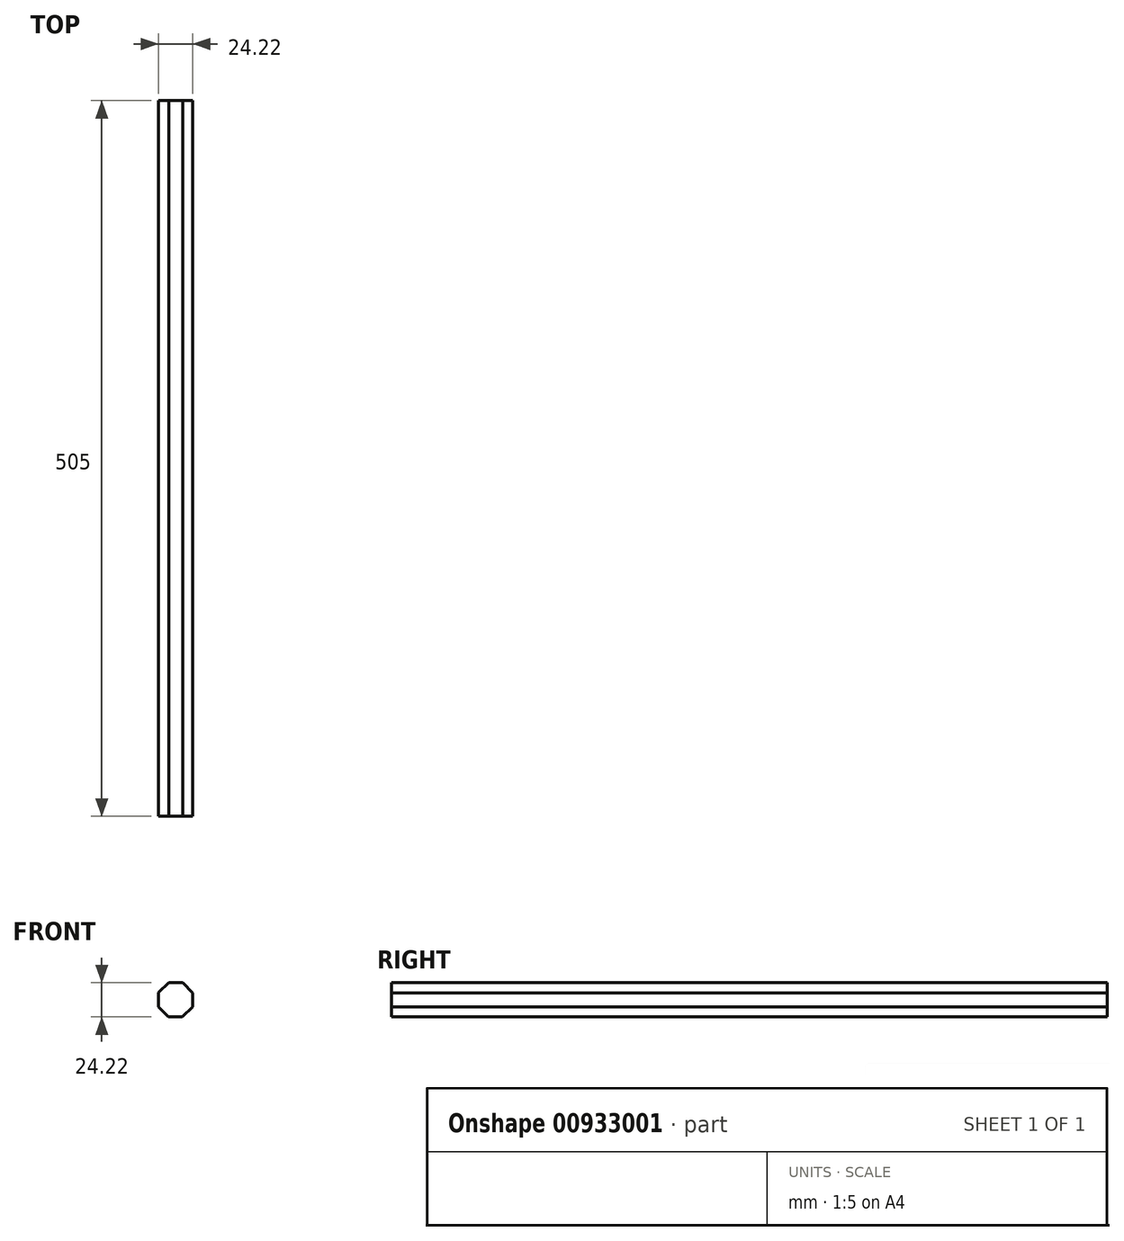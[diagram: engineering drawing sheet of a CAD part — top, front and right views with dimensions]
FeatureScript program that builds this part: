
annotation { "Feature Type Name" : "Feature", "Feature Type Description" : "" }
export const myFeature = defineFeature(function(context is Context, id is Id, definition is map)
    precondition{}
    {
        {
            var Q0;
            Q0=qCreatedBy(makeId("Front.planeOp"),FACE);
            var sketch = newSketch(context, id + "F0", { "sketchPlane" : qUnion([Q0])});
            skCircle(sketch, "E0.cCircle", {"center": v(0, 0) * mm, "radius": 12.07 * mm, "construction": true});
            skLineSegment(sketch, "E0.0", {"start": v(12.03, -5.1) * mm, "end": v(4.9, -12.1) * mm});
            skLineSegment(sketch, "E0.1", {"start": v(4.9, -12.1) * mm, "end": v(-5.1, -12.03) * mm});
            skLineSegment(sketch, "E0.2", {"start": v(-5.1, -12.03) * mm, "end": v(-12.1, -4.9) * mm});
            skLineSegment(sketch, "E0.3", {"start": v(-12.1, -4.9) * mm, "end": v(-12.03, 5.1) * mm});
            skLineSegment(sketch, "E0.4", {"start": v(-12.03, 5.1) * mm, "end": v(-4.9, 12.1) * mm});
            skLineSegment(sketch, "E0.5", {"start": v(-4.9, 12.1) * mm, "end": v(5.1, 12.03) * mm});
            skLineSegment(sketch, "E0.6", {"start": v(5.1, 12.03) * mm, "end": v(12.1, 4.9) * mm});
            skLineSegment(sketch, "E0.7", {"start": v(12.1, 4.9) * mm, "end": v(12.03, -5.1) * mm});
            skPoint(sketch, "E0.0.midPoint", {"position": v(8.47, -8.6) * mm});
            skSolve(sketch);
        }
        {
            var Q0;
            Q0 = qSketchRegion(id + "F0", true);
            extrude(context, id + "F1", {"entities" : qUnion([Q0]), "depth" : 505 * mm, "offsetDistance" : 25 * mm});
        }
        {
            var Q0;
            Q0=makeQuery(id+"F1.opExtrude","SWEPT_FACE",FACE,{"disambiguationData":[OSD([sQuery(id+"F0.wireOp",EDGE,"E0.5")])]});
            var sketch = newSketch(context, id + "F2", { "sketchPlane" : qUnion([Q0])});
            skSolve(sketch);
        }
        {
            var Q0;
            Q0=makeQuery(id+"F1.opExtrude","SWEPT_BODY",BODY,{"disambiguationData":[OSD([sQuery(id+"F0.wireOp",EDGE,"E0.0"),sQuery(id+"F0.wireOp",EDGE,"E0.1"),sQuery(id+"F0.wireOp",EDGE,"E0.2"),sQuery(id+"F0.wireOp",EDGE,"E0.3"),sQuery(id+"F0.wireOp",EDGE,"E0.4"),sQuery(id+"F0.wireOp",EDGE,"E0.5"),sQuery(id+"F0.wireOp",EDGE,"E0.6"),sQuery(id+"F0.wireOp",EDGE,"E0.7")])]});
            transform(context, id + "F3", {"entities" : qUnion([Q0]), "transformType" : TransformType.TRANSLATION_3D, "dx" : 0 * mm, "dy" : 0 * mm, "dz" : 0 * mm, "makeCopy" : true});
        }
    });
